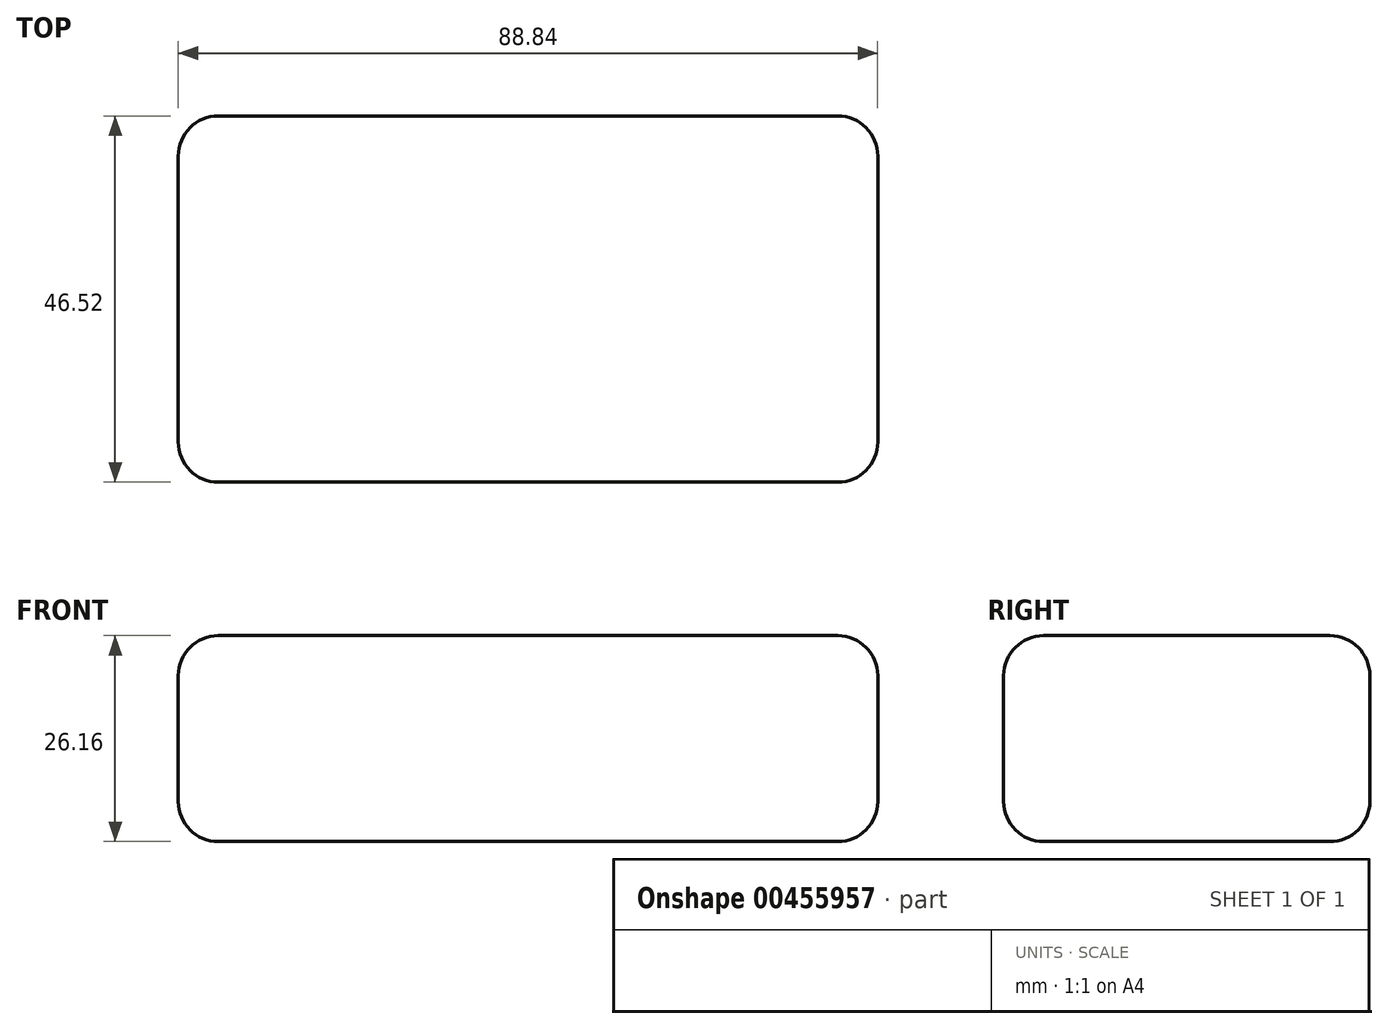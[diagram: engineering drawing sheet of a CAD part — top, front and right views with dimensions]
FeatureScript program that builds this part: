
annotation { "Feature Type Name" : "Feature", "Feature Type Description" : "" }
export const myFeature = defineFeature(function(context is Context, id is Id, definition is map)
    precondition{}
    {
        {
            var Q0;
            Q0=qCreatedBy(makeId("Top.planeOp"),FACE);
            var sketch = newSketch(context, id + "F0", { "sketchPlane" : qUnion([Q0])});
            skLineSegment(sketch, "E0.bottom", {"start": v(44.42, 23.26) * mm, "end": v(-44.42, 23.26) * mm});
            skLineSegment(sketch, "E0.top", {"start": v(44.42, -23.26) * mm, "end": v(-44.42, -23.26) * mm});
            skLineSegment(sketch, "E0.left", {"start": v(44.42, 23.26) * mm, "end": v(44.42, -23.26) * mm});
            skLineSegment(sketch, "E0.right", {"start": v(-44.42, 23.26) * mm, "end": v(-44.42, -23.26) * mm});
            skPoint(sketch, "E0.middle", {"position": v(0, 0) * mm});
            skSolve(sketch);
        }
        {
            var Q0;
            Q0 = qSketchRegion(id + "F0", true);
            extrude(context, id + "F1", {"entities" : qUnion([Q0]), "depth" : 26.16 * mm});
        }
        {
            var Q0;
            Q0=makeQuery(id+"F1.opExtrude","SWEPT_FACE",FACE,{"disambiguationData":[OSD([sQuery(id+"F0.wireOp",EDGE,"E0.top")])]});
            var Q1;
            Q1=makeQuery(id+"F1.opExtrude","CAP_FACE",FACE,{"disambiguationData":[OSD([sQuery(id+"F0.wireOp",EDGE,"E0.bottom"),sQuery(id+"F0.wireOp",EDGE,"E0.top"),sQuery(id+"F0.wireOp",EDGE,"E0.left"),sQuery(id+"F0.wireOp",EDGE,"E0.right")])],"isStart":false});
            var Q2;
            Q2=makeQuery(id+"F1.opExtrude","SWEPT_FACE",FACE,{"disambiguationData":[OSD([sQuery(id+"F0.wireOp",EDGE,"E0.left")])]});
            var Q3;
            Q3=makeQuery(id+"F1.opExtrude","CAP_FACE",FACE,{"disambiguationData":[OSD([sQuery(id+"F0.wireOp",EDGE,"E0.bottom"),sQuery(id+"F0.wireOp",EDGE,"E0.top"),sQuery(id+"F0.wireOp",EDGE,"E0.left"),sQuery(id+"F0.wireOp",EDGE,"E0.right")])],"isStart":true});
            var Q4;
            Q4=makeQuery(id+"F1.opExtrude","SWEPT_FACE",FACE,{"disambiguationData":[OSD([sQuery(id+"F0.wireOp",EDGE,"E0.bottom")])]});
            var Q5;
            Q5=makeQuery(id+"F1.opExtrude","CAP_EDGE",EDGE,{"disambiguationData":[OSD([sQuery(id+"F0.wireOp",EDGE,"E0.right")])],"isStart":false});
            fillet(context, id + "F2", {"entities" : qUnion([Q0, Q1, Q2, Q3, Q4, Q5]), "radius" : 5.08 * mm, "tangentPropagation" : true, "allowEdgeOverflow" : false});
        }
    });
